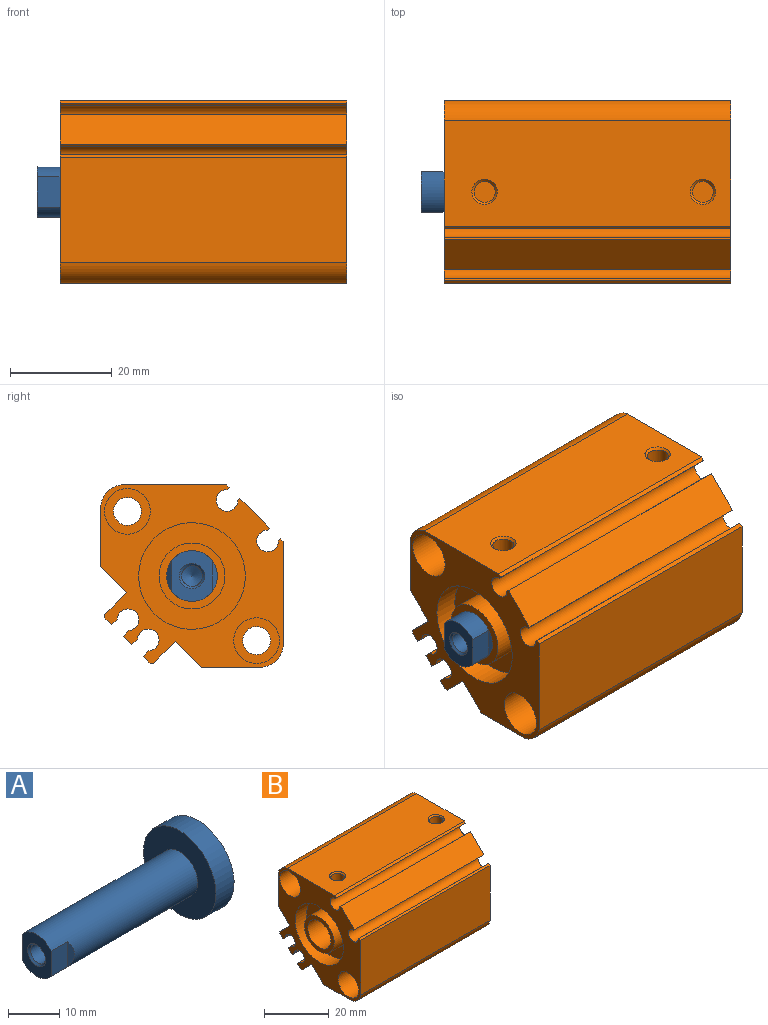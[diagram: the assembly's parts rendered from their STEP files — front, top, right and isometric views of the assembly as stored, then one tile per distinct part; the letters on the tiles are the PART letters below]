
ASSEMBLY  parts=2 mates=1
PART A: 12 faces, bbox 44.5x20x20 mm
  f0: cone r=866.03mm half-angle=60deg, axis (-1,0,0), area 15.5mm2, adj f1
  f1: cylinder r=2.07mm len=6.57mm, axis (-1,0,0), area 85.3mm2, adj f0,f4
  f2: cylinder r=5mm len=39.5mm, axis (-1,0,0), area 1174.5mm2, adj f3,f5,f8,f9,f10,f11
  f3: plane 10x8mm, normal (-1,0,0), area 50.7mm2, adj f2,f4,f9,f10
  f4: cone r=2.07mm half-angle=45deg, axis (-1,0,0), area 8.8mm2, adj f1,f3
  f5: plane 20x20mm, normal (-1,0,0), area 235.6mm2, adj f2,f6
  f6: cylinder r=10mm len=20mm, axis (-1,0,0), area 314.2mm2, adj f5,f7
  f7: plane 20x20mm, normal (1,0,0), area 314.2mm2, adj f6
  f8: plane 6x1mm, normal (-0.71,-0.71,0), area 5.8mm2, adj f2,f9
  f9: plane 6x4.5mm, normal (0,-1,0), area 27mm2, adj f2,f3,f8
  f10: plane 6x4.5mm, normal (0,1,0), area 27mm2, adj f2,f3,f11
  f11: plane 6x1mm, normal (-0.71,0.71,0), area 5.8mm2, adj f2,f10
PART B: 58 faces, bbox 56.5x36x36 mm
  f0: plane 56.5x0.42mm, normal (0,0.71,0.71), area 33.2mm2, adj f1,f2,f3,f34
  f1: plane 36x36mm, normal (1,0,0), area 576.8mm2, adj f0,f2,f3,f4,f5,f6,f7,f8
  f2: cylinder r=2.13mm len=56.5mm, axis (1,0,0), area 568.1mm2, adj f0,f1,f30,f34
  f3: plane 56.5x0.57mm, normal (0,-0.71,0.71), area 45.5mm2, adj f0,f1,f4,f34
  f4: plane 56.5x20.73mm, normal (0,-1,0), area 1171.2mm2, adj f1,f3,f5,f34
  f5: cylinder r=5mm len=56.5mm, axis (1,0,0), area 341.6mm2, adj f1,f4,f6,f34
  f6: plane 56.5x12.1mm, normal (0,0,-1), area 683.8mm2, adj f1,f5,f7,f34
  f7: plane 56.5x5.13mm, normal (0,0.71,-0.71), area 410mm2, adj f1,f6,f8,f34
  f8: plane 56.5x4.31mm, normal (0,-0.71,-0.71), area 344.7mm2, adj f1,f7,f9,f34
  f9: plane 56.5x0.71mm, normal (0,0,-1), area 40mm2, adj f1,f8,f10,f34
  f10: plane 56.5x1.34mm, normal (0,0.71,-0.71), area 107.4mm2, adj f1,f9,f11,f34
  f11: plane 56.5x1.13mm, normal (0,0.71,0.71), area 90.1mm2, adj f1,f10,f12,f34
  f12: cylinder r=2.13mm len=56.5mm, axis (1,0,0), area 551.6mm2, adj f1,f11,f13,f34
  f13: plane 56.5x1.13mm, normal (0,-0.71,-0.71), area 90.1mm2, adj f1,f12,f14,f34
  f14: plane 56.5x1.7mm, normal (0,0.71,-0.71), area 135.6mm2, adj f1,f13,f15,f34
  f15: plane 56.5x1.13mm, normal (0,0.71,0.71), area 90.1mm2, adj f1,f14,f16,f34
  f16: cylinder r=2.13mm len=56.5mm, axis (1,0,0), area 551.6mm2, adj f1,f15,f17,f34
  f17: plane 56.5x1.13mm, normal (0,-0.71,-0.71), area 90.1mm2, adj f1,f16,f18,f34
  f18: plane 56.5x1.34mm, normal (0,0.71,-0.71), area 107.4mm2, adj f1,f17,f19,f34
  f19: plane 56.5x0.71mm, normal (0,1,0), area 40mm2, adj f1,f18,f20,f34
  f20: plane 56.5x4.31mm, normal (0,0.71,0.71), area 344.7mm2, adj f1,f19,f21,f34
  f21: plane 56.5x5.13mm, normal (0,0.71,-0.71), area 410mm2, adj f1,f20,f22,f34
  f22: plane 56.5x12.1mm, normal (0,1,0), area 683.8mm2, adj f1,f21,f23,f34
  f23: cylinder r=5mm len=56.5mm, axis (1,0,0), area 341.6mm2, adj f1,f22,f24,f34
  f24: plane 56.5x20.73mm, normal (0,0,1), area 1131.9mm2, adj f1,f23,f25,f34,f42,f45
  f25: plane 56.5x0.57mm, normal (0,-0.71,0.71), area 45.5mm2, adj f1,f24,f26,f34
  f26: plane 56.5x0.42mm, normal (0,-0.71,-0.71), area 33.2mm2, adj f1,f25,f27,f34
  f27: cylinder r=2.13mm len=56.5mm, axis (1,0,0), area 568.1mm2, adj f1,f26,f28,f34
  f28: plane 56.5x0.42mm, normal (0,0.71,0.71), area 33.2mm2, adj f1,f27,f29,f34
  f29: plane 56.5x5.87mm, normal (0,-0.71,0.71), area 468.9mm2, adj f1,f28,f30,f34
  f30: plane 56.5x0.42mm, normal (0,-0.71,-0.71), area 33.2mm2, adj f1,f2,f29,f34
  f31: cylinder r=10.5mm len=21mm, axis (-1,0,0), area 131.9mm2, adj f1,f33
  f32: cylinder r=6.5mm len=13mm, axis (1,0,0), area 204.2mm2, adj f35,f37
  f33: plane 21x21mm, normal (1,0,0), area 346.4mm2, adj f31
  f34: plane 36x36mm, normal (-1,0,0), area 576.8mm2, adj f0,f2,f3,f4,f5,f6,f7,f8
  f35: plane 13x13mm, normal (-1,0,0), area 54.2mm2, adj f32,f36
  f36: cylinder r=5mm len=10mm, axis (-1,0,0), area 314.2mm2, adj f35,f39
  f37: plane 21x21mm, normal (-1,0,0), area 213.6mm2, adj f32,f38
  f38: cylinder r=10.5mm len=21mm, axis (1,0,0), area 329.9mm2, adj f34,f37
  f39: plane 20x20mm, normal (1,0,0), area 235.6mm2, adj f36,f40
  f40: cylinder r=10mm len=30mm, axis (-1,0,0), area 1885mm2, adj f39,f41
  f41: plane 20x20mm, normal (-1,0,0), area 314.2mm2, adj f40
  f42: cone r=2.5mm half-angle=45deg, axis (0,0,1), area 8.8mm2, adj f24,f43
  f43: cylinder r=2.07mm len=5.57mm, axis (0,0,1), area 72.3mm2, adj f42,f44
  f44: plane 4.13x4.13mm, normal (0,0,1), area 13.4mm2, adj f43
  f45: cone r=2.5mm half-angle=45deg, axis (0,0,1), area 8.8mm2, adj f24,f46
  f46: cylinder r=2.07mm len=5.57mm, axis (0,0,1), area 72.3mm2, adj f45,f47
  f47: plane 4.13x4.13mm, normal (0,0,1), area 13.4mm2, adj f46
  f48: cylinder r=4.5mm len=9mm, axis (-1,0,0), area 197.9mm2, adj f34,f49
  f49: plane 9x9mm, normal (-1,0,0), area 39.9mm2, adj f48,f50
  f50: cylinder r=2.75mm len=42.5mm, axis (-1,0,0), area 734.3mm2, adj f49,f51
  f51: plane 9x9mm, normal (1,0,0), area 39.9mm2, adj f50,f52
  f52: cylinder r=4.5mm len=9mm, axis (-1,0,0), area 197.9mm2, adj f1,f51
  f53: cylinder r=4.5mm len=9mm, axis (-1,0,0), area 197.9mm2, adj f34,f54
  f54: plane 9x9mm, normal (-1,0,0), area 39.9mm2, adj f53,f55
  f55: cylinder r=2.75mm len=42.5mm, axis (-1,0,0), area 734.3mm2, adj f54,f56
  f56: plane 9x9mm, normal (1,0,0), area 39.9mm2, adj f55,f57
  f57: cylinder r=4.5mm len=9mm, axis (-1,0,0), area 197.9mm2, adj f1,f56
PLACE A at identity
PLACE B at identity
MATE slider B.f32 <-> A.f0  axis (-1,0,0) through (40,0,0)mm
